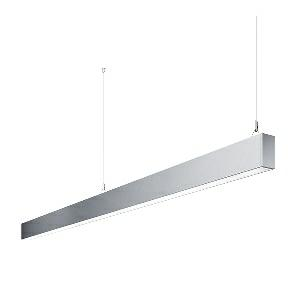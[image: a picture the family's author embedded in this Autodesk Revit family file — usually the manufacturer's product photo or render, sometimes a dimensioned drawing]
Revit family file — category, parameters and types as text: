
# Revit family: idoo_line_-_ilp_6000_840_d_end_00805707_898d
name_source: partatom
category: Lighting Fixtures
units: mm (PartAtom-declared; Revit-internal decimal feet)

## family parameters
Cut with Voids When Loaded = No
Host = Face
Light Source = No
Part Type = Normal
Room Calculation Point = No
Round Connector Dimension = Use Diameter
Shared = No

## types (1)
- IDOO.line - ILP 6000/840/D END (1 x LED, 6300 lm, 4000K)
    Apparent Load = 46 VA
    Approval mark = CE
    CIE Flux Codes = 66 91 98 40 100
    Color Rendering = 80-89
    Color Temperature = 4000K
    Control Gear = Electronic ballast
    Default Elevation = 1800 mm
    Description = ILP 6000/840/D|Suspended luminaire|light source: LED|connected load: 220-240 V, 50/60 Hz|Power consumption: approx. 46 W|standby: approx. 0,15|luminous flux: 6300 lm|luminous efficacy: 136 lm/W|light distribution: Direct/indirect|direct ratio: approx. 40 %|colour temperature: Cold white, ca. 4000 K|color rendering index (CRI): >= 80|chromaticity tolerance:  3 SDCM|System of protection: IP 40|technology: Continuously dimmable|luminaire body|material: Sectional aluminium|colour: Silver|lamp cover: Acrylic (PMMA), Clear|mains lead: 1,0 m With free stranded wires|Fastening: Steel cable 0.3 - 0.7 m|glare control: Prism aperture|luminance(L65): <= 2700 cd/m|unified glare rating(4H 8H): <=  16|special features: DALI Load 1x, TouchDIM - dimming via standard switch, Through-wired, up to 18 m on one mains connection, Flicker-free, Suitable as emergency lighting, Mechanical and electrical connection of the individual modules without tools|
    Frequency = 50 Hz
    Height = 110 mm
    Lamp = 1 x LED
    Lamp Light Flux = 6300 lm
    Lamp count = 1
    Length = 2250 mm
    Luminous efficacy = 137 lm/W
    Manufacturer = Waldmann
    ModVariant = No
    Model = 00805707
    Mounting Place = Ceiling
    Mounting Type = Pendant
    Number of Poles = 1
    OnlyDefault = Yes
    Power Factor = 1
    Product Name = IDOO.line - ILP 6000/840/D END
    Product group = Suspended luminaire
    ProductGroupID = 9
    Protection Class = Protection class I
    Protection Degree = IP 40
    RLX_Detail_Level = 1
    RLX_Emergency_Light_Flux = 0 lm
    RLX_Emergency_Type = 0
    RLX_Emergency_Type_DB = No
    RlxData = <blob elided: 22861 chars, md5=b6b8415c>
    Socket = socket
    Standby Power = 0 W
    System Light Flux = 6300 lm
    System Power = 46 W
    Type Comments = Product without accessories
    Type Image = 113318000-00692621.jpg
    URL = http://relux.com
    VarID = ---
    Voltage = 230 V
    Voltage Range = 220-240 V
    Weight = 0.00 kg
    Width = 60 mm  [stored 0.19685 ft]

note: [stored X ft] marks values corroborated as IEEE doubles in the binary element streams (Revit-internal decimal feet)

## geometry (parser evidence)
native form markers: Blend x4, Sweep x17
no freeform markers — native parametric forms only
